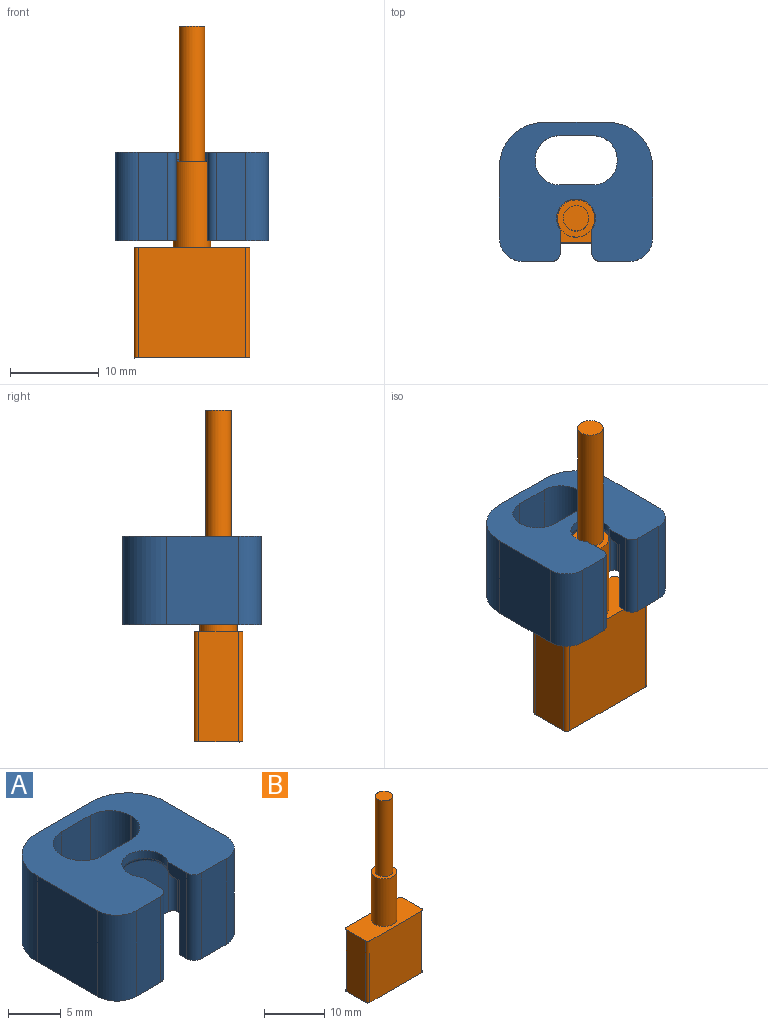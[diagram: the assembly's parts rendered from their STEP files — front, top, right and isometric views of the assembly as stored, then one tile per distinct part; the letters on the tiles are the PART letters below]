
ASSEMBLY  parts=2 mates=1
PART A: 43 faces, bbox 17.3x15.7x10 mm
  f0: plane 10x3.3mm, normal (0,-1,0), area 33mm2, adj f2,f15,f19,f41
  f1: plane 8.6x4.3mm, normal (0,1,0), area 37mm2, adj f7,f19,f20,f22
  f2: plane 17.3x15.7mm, normal (0,0,1), area 187.1mm2, adj f0,f11,f12,f13,f14,f15,f16,f17
  f3: plane 8.6x4.5mm, normal (-1,0,0), area 38.7mm2, adj f7,f10,f19,f20
  f4: plane 8.6x4.3mm, normal (0,1,0), area 37mm2, adj f8,f19,f20,f23
  f5: plane 8.6x4.5mm, normal (1,0,0), area 38.7mm2, adj f8,f9,f19,f20
  f6: plane 12.1x8.6mm, normal (0,-1,0), area 104.1mm2, adj f9,f10,f19,f20
  f7: cylinder r=0.6mm len=8.6mm, axis (0,0,-1), area 8.1mm2, adj f1,f3,f19,f20
  f8: cylinder r=0.6mm len=8.6mm, axis (0,0,-1), area 8.1mm2, adj f4,f5,f19,f20
  f9: cylinder r=0.6mm len=8.6mm, axis (0,0,-1), area 8.1mm2, adj f5,f6,f19,f20
  f10: cylinder r=0.6mm len=8.6mm, axis (0,0,-1), area 8.1mm2, adj f3,f6,f19,f20
  f11: plane 9.5x0.15mm, normal (1,0,0), area 1.4mm2, adj f2,f28,f31,f35
  f12: plane 10x8.1mm, normal (-1,0,0), area 81mm2, adj f2,f13,f19,f27
  f13: cylinder r=2.6mm len=10mm, axis (0,0,-1), area 40.8mm2, adj f2,f12,f14,f19
  f14: plane 10x3.3mm, normal (0,-1,0), area 33mm2, adj f2,f13,f19,f40
  f15: cylinder r=2.6mm len=10mm, axis (0,0,-1), area 40.8mm2, adj f0,f2,f16,f19
  f16: plane 10x8.1mm, normal (1,0,0), area 81mm2, adj f2,f15,f19,f25
  f17: plane 9.5x0.15mm, normal (-1,0,0), area 1.4mm2, adj f2,f29,f30,f36
  f18: plane 9.5x3.85mm, normal (0,1,0), area 36.6mm2, adj f2,f30,f31,f32
  f19: plane 17.3x15.7mm, normal (0,0,-1), area 116.7mm2, adj f0,f1,f3,f4,f5,f6,f7,f8
  f20: plane 13.3x5.7mm, normal (0,0,-1), area 51.4mm2, adj f1,f3,f4,f5,f6,f7,f8,f9
  f21: cylinder r=2.2mm len=4.4mm, axis (0,0,-1), area 8.8mm2, adj f2,f22,f23,f42
  f22: plane 10x2.52mm, normal (-1,0,0), area 12mm2, adj f1,f2,f19,f20,f21,f41,f42
  f23: plane 10x2.52mm, normal (1,0,0), area 12mm2, adj f2,f4,f19,f20,f21,f40,f42
  f24: plane 9.5x3.85mm, normal (0,-1,0), area 36.6mm2, adj f2,f28,f29,f39
  f25: cylinder r=5mm len=10mm, axis (0,0,-1), area 78.5mm2, adj f2,f16,f19,f26
  f26: plane 10x7.3mm, normal (0,1,0), area 73mm2, adj f2,f19,f25,f27
  f27: cylinder r=5mm len=10mm, axis (0,0,-1), area 78.5mm2, adj f2,f12,f19,f26
  f28: cylinder r=2.7mm len=9.5mm, axis (0,0,-1), area 40.3mm2, adj f2,f11,f24,f37
  f29: cylinder r=2.7mm len=9.5mm, axis (0,0,1), area 40.3mm2, adj f2,f17,f24,f38
  f30: cylinder r=2.7mm len=9.5mm, axis (0,0,-1), area 40.3mm2, adj f2,f17,f18,f34
  f31: cylinder r=2.7mm len=9.5mm, axis (0,0,1), area 40.3mm2, adj f2,f11,f18,f33
  f32: cylinder r=0.5mm len=3.85mm, axis (-1,0,0), area 3mm2, adj f18,f19,f33,f34
  f33: torus R=3.2mm, axis (0,0,1), area 3.6mm2, adj f19,f31,f32,f35
  f34: torus R=3.2mm, axis (0,0,1), area 3.6mm2, adj f19,f30,f32,f36
  f35: cylinder r=0.5mm len=0.5mm, axis (0,1,0), area 0.1mm2, adj f11,f19,f33,f37
  f36: cylinder r=0.5mm len=0.5mm, axis (0,-1,0), area 0.1mm2, adj f17,f19,f34,f38
  f37: torus R=3.2mm, axis (0,0,1), area 3.6mm2, adj f19,f28,f35,f39
  f38: torus R=3.2mm, axis (0,0,1), area 3.6mm2, adj f19,f29,f36,f39
  f39: cylinder r=0.5mm len=3.85mm, axis (1,0,0), area 3mm2, adj f19,f24,f37,f38
  f40: cylinder r=1mm len=10mm, axis (0,0,1), area 15.7mm2, adj f2,f14,f19,f23
  f41: cylinder r=1mm len=10mm, axis (0,0,-1), area 15.7mm2, adj f0,f2,f19,f22
  f42: torus R=2.7mm, axis (0,0,1), area 8.7mm2, adj f20,f21,f22,f23
PART B: 14 faces, bbox 13.1x5.5x37.5 mm
  f0: plane 12.5x12.1mm, normal (0,1,0), area 151.3mm2, adj f1,f7,f8,f9
  f1: cylinder r=0.5mm len=12.5mm, axis (0,0,-1), area 9.8mm2, adj f0,f2,f8,f9
  f2: plane 12.5x4.5mm, normal (-1,0,0), area 56.2mm2, adj f1,f3,f8,f9
  f3: cylinder r=0.5mm len=12.5mm, axis (0,0,-1), area 9.8mm2, adj f2,f4,f8,f9
  f4: plane 12.5x12.1mm, normal (0,-1,0), area 151.3mm2, adj f3,f5,f8,f9
  f5: cylinder r=0.5mm len=12.5mm, axis (0,0,-1), area 9.8mm2, adj f4,f6,f8,f9
  f6: plane 12.5x4.5mm, normal (1,0,0), area 56.2mm2, adj f5,f7,f8,f9
  f7: cylinder r=0.5mm len=12.5mm, axis (0,0,-1), area 9.8mm2, adj f0,f6,f8,f9
  f8: plane 13.1x5.5mm, normal (0,0,1), area 58mm2, adj f0,f1,f2,f3,f4,f5,f6,f7
  f9: plane 13.1x5.5mm, normal (0,0,-1), area 71.8mm2, adj f0,f1,f2,f3,f4,f5,f6,f7
  f10: cylinder r=2.1mm len=9.65mm, axis (0,0,-1), area 127.3mm2, adj f8,f11
  f11: plane 4.2x4.2mm, normal (0,0,1), area 7.4mm2, adj f10,f12
  f12: cylinder r=1.44mm len=15.35mm, axis (0,0,-1), area 138.4mm2, adj f11,f13
  f13: plane 2.87x2.87mm, normal (0,0,1), area 6.5mm2, adj f12
PLACE A rot(axis=(0.28,-0.96,0.05),0deg) t=(-10.95,1.22,2.57)mm
PLACE B rot(axis=(0.28,-0.96,0.05),0deg) t=(-10.95,1.22,-6.7)mm fixed
MATE slider B.f10 <-> A.f21  axis (0,0,1) through (-10.95,1.22,5.8)mm
